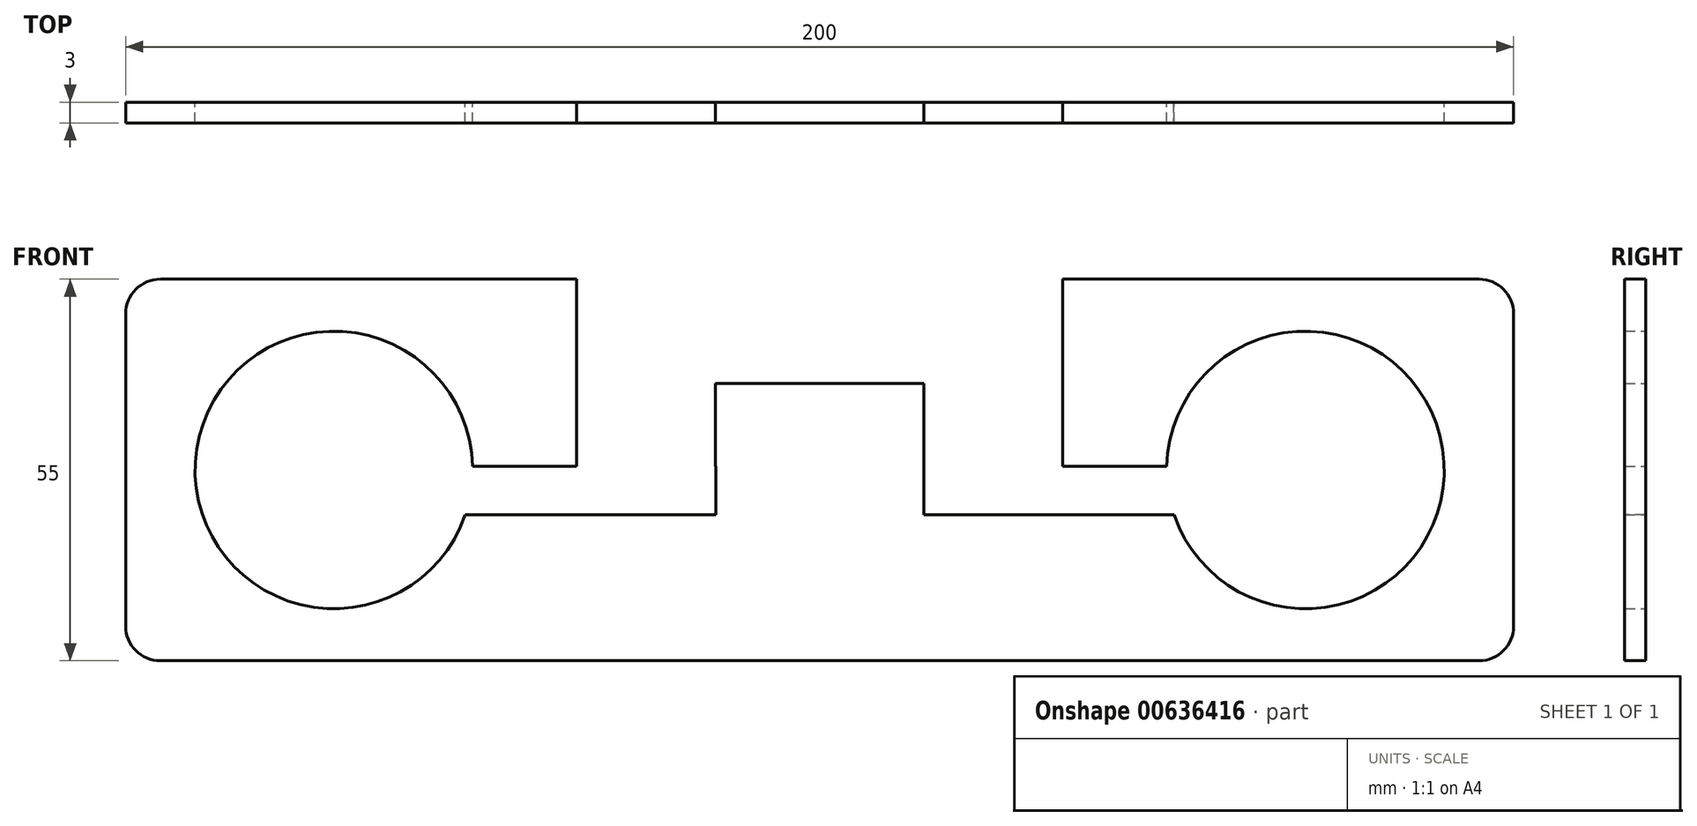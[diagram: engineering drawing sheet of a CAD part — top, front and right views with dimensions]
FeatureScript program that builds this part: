
annotation { "Feature Type Name" : "Feature", "Feature Type Description" : "" }
export const myFeature = defineFeature(function(context is Context, id is Id, definition is map)
    precondition{}
    {
        {
            var Q0;
            Q0=qCreatedBy(makeId("Front.planeOp"),FACE);
            var sketch = newSketch(context, id + "F0", { "sketchPlane" : qUnion([Q0])});
            skLineSegment(sketch, "E0.bottom", {"start": v(-79.88, 47.92) * mm, "end": v(110.12, 47.92) * mm});
            skLineSegment(sketch, "E0.top", {"start": v(-79.88, -7.08) * mm, "end": v(110.12, -7.08) * mm});
            skLineSegment(sketch, "E0.left", {"start": v(-84.88, 42.92) * mm, "end": v(-84.88, -2.08) * mm});
            skLineSegment(sketch, "E0.right", {"start": v(115.12, 42.92) * mm, "end": v(115.12, -2.08) * mm});
            skPoint(sketch, "E1.visualSharp", {"position": v(-84.88, 47.92) * mm});
            skArc(sketch, "E1.filletArc", {"start": v(-79.88, 47.92) * mm, "mid": v(-83.41, 46.45) * mm, "end": v(-84.88, 42.92) * mm});
            skPoint(sketch, "E2.visualSharp", {"position": v(115.12, 47.92) * mm});
            skArc(sketch, "E2.filletArc", {"start": v(115.12, 42.92) * mm, "mid": v(113.66, 46.45) * mm, "end": v(110.12, 47.92) * mm});
            skPoint(sketch, "E3.visualSharp", {"position": v(115.12, -7.08) * mm});
            skArc(sketch, "E3.filletArc", {"start": v(110.12, -7.08) * mm, "mid": v(113.66, -5.62) * mm, "end": v(115.12, -2.08) * mm});
            skPoint(sketch, "E4.visualSharp", {"position": v(-84.88, -7.08) * mm});
            skArc(sketch, "E4.filletArc", {"start": v(-84.88, -2.08) * mm, "mid": v(-83.41, -5.62) * mm, "end": v(-79.88, -7.08) * mm});
            skCircle(sketch, "E5", {"center": v(-54.88, 20.42) * mm, "radius": 20 * mm});
            skCircle(sketch, "E6", {"center": v(85.12, 20.42) * mm, "radius": 20 * mm});
            skSolve(sketch);
        }
        {
            var Q0;
            Q0=makeQuery(id+"F0.imprint","IMPRINT",FACE,{"disambiguationData":[TD([[makeQuery(id+"F0.imprint","IMPRINT",EDGE,{"derivedFrom":sQuery(id+"F0.wireOp",EDGE,"E0.bottom")}),-1.0]])]});
            extrude(context, id + "F1", {"entities" : qUnion([Q0]), "depth" : 3 * mm, "offsetDistance" : 25 * mm});
        }
        {
            var Q0;
            Q0=makeQuery(id+"F1.opExtrude","CAP_FACE",FACE,{"disambiguationData":[OSD([sQuery(id+"F0.wireOp",EDGE,"E0.bottom"),sQuery(id+"F0.wireOp",EDGE,"E0.top"),sQuery(id+"F0.wireOp",EDGE,"E0.left"),sQuery(id+"F0.wireOp",EDGE,"E0.right"),sQuery(id+"F0.wireOp",EDGE,"E1.filletArc"),sQuery(id+"F0.wireOp",EDGE,"E2.filletArc"),sQuery(id+"F0.wireOp",EDGE,"E3.filletArc"),sQuery(id+"F0.wireOp",EDGE,"E4.filletArc"),sQuery(id+"F0.wireOp",EDGE,"E5"),sQuery(id+"F0.wireOp",EDGE,"E6")])],"isStart":false});
            var sketch = newSketch(context, id + "F2", { "sketchPlane" : qUnion([Q0])});
            skLineSegment(sketch, "E7", {"start": v(-19.88, 47.92) * mm, "end": v(-19.88, 73.58) * mm});
            skLineSegment(sketch, "E8", {"start": v(50.12, 47.92) * mm, "end": v(50.12, 77.54) * mm});
            skSolve(sketch);
        }
        {
            var Q0;
            Q0=makeQuery(id+"F1.opExtrude","SWEPT_FACE",FACE,{"disambiguationData":[OSD([sQuery(id+"F0.wireOp",EDGE,"E0.bottom")])]});
            var sketch = newSketch(context, id + "F3", { "sketchPlane" : qUnion([Q0])});
            skLineSegment(sketch, "E9", {"start": v(-19.88, -3) * mm, "end": v(-19.88, 0) * mm});
            skLineSegment(sketch, "E10", {"start": v(50.12, -3) * mm, "end": v(50.12, 0) * mm});
            skSolve(sketch);
        }
        {
            var Q0;
            {var subQ0=sQuery(id+"F3.wireOp",EDGE,"E9");Q0=makeQuery(id+"F3.imprint","IMPRINT",FACE,{"disambiguationData":[TD([[makeQuery(id+"F3.imprint","IMPRINT",EDGE,{"derivedFrom":subQ0}),-1.0]])]});}
            extrude(context, id + "F4", {"entities" : qUnion([Q0]), "operationType" : NewBodyOperationType.REMOVE, "oppositeDirection" : true, "depth" : 15 * mm, "offsetDistance" : 25 * mm});
        }
        {
            var Q0;
            Q0=makeQuery(id+"F4.boolean.opBoolean","COPY",FACE,{"derivedFrom":makeQuery(id+"F4.opExtrude","CAP_FACE",FACE,{"disambiguationData":[OSD([sQuery(id+"F0.wireOp",EDGE,"E0.bottom"),sQuery(id+"F3.wireOp",EDGE,"E9"),sQuery(id+"F3.wireOp",EDGE,"E10")])],"isStart":false})});
            var sketch = newSketch(context, id + "F5", { "sketchPlane" : qUnion([Q0])});
            skLineSegment(sketch, "E11", {"start": v(0.12, -3) * mm, "end": v(0.12, 0) * mm});
            skLineSegment(sketch, "E12", {"start": v(30.12, 0) * mm, "end": v(30.12, -3) * mm});
            skSolve(sketch);
        }
        {
            var Q0;
            {var subQ0=sQuery(id+"F5.wireOp",EDGE,"E11");Q0=makeQuery(id+"F5.imprint","IMPRINT",FACE,{"disambiguationData":[TD([[makeQuery(id+"F5.imprint","IMPRINT",EDGE,{"derivedFrom":subQ0}),1.0]])]});}
            var Q1;
            {var subQ0=sQuery(id+"F5.wireOp",EDGE,"E12");Q1=makeQuery(id+"F5.imprint","IMPRINT",FACE,{"disambiguationData":[TD([[makeQuery(id+"F5.imprint","IMPRINT",EDGE,{"derivedFrom":subQ0}),1.0]])]});}
            extrude(context, id + "F6", {"entities" : qUnion([Q0, Q1]), "operationType" : NewBodyOperationType.REMOVE, "oppositeDirection" : true, "depth" : 12 * mm, "offsetDistance" : 25 * mm});
        }
        {
            var Q0;
            Q0=makeQuery(id+"F2.imprint","IMPRINT",FACE,{"disambiguationData":[TD([[makeQuery(id+"F2.imprint","IMPRINT",EDGE,{"derivedFrom":makeQuery(id+"F1.opExtrude","CAP_EDGE",EDGE,{"disambiguationData":[OSD([sQuery(id+"F0.wireOp",EDGE,"E0.top")])],"isStart":false})}),1.0]])]});
            var sketch = newSketch(context, id + "F7", { "sketchPlane" : qUnion([Q0])});
            skLineSegment(sketch, "E13", {"start": v(-19.86, 20.93) * mm, "end": v(-34.91, 20.93) * mm});
            skLineSegment(sketch, "E14", {"start": v(0.13, 20.94) * mm, "end": v(0.13, 13.94) * mm});
            skLineSegment(sketch, "E15", {"start": v(0.13, 13.94) * mm, "end": v(-36.02, 13.94) * mm});
            skLineSegment(sketch, "E16", {"start": v(50.12, 20.93) * mm, "end": v(65.14, 20.93) * mm});
            skLineSegment(sketch, "E17", {"start": v(30.12, 20.92) * mm, "end": v(30.12, 13.93) * mm});
            skLineSegment(sketch, "E18", {"start": v(30.12, 13.93) * mm, "end": v(66.08, 13.93) * mm});
            skLineSegment(sketch, "E19", {"start": v(-19.86, 20.93) * mm, "end": v(0.13, 20.94) * mm});
            skLineSegment(sketch, "E20", {"start": v(30.12, 20.92) * mm, "end": v(50.12, 20.93) * mm});
            skLineSegment(sketch, "E21", {"start": v(65.14, 20.93) * mm, "end": v(73.13, 16.83) * mm});
            skLineSegment(sketch, "E22", {"start": v(73.13, 16.83) * mm, "end": v(66.08, 13.93) * mm});
            skLineSegment(sketch, "E23", {"start": v(-34.91, 20.93) * mm, "end": v(-38.79, 20.93) * mm});
            skLineSegment(sketch, "E24", {"start": v(-38.79, 20.93) * mm, "end": v(-36.02, 13.94) * mm});
            skSolve(sketch);
        }
        {
            var Q0;
            Q0=qSketchRegion(id+"F7",true);
            extrude(context, id + "F8", {"entities" : qUnion([Q0]), "operationType" : NewBodyOperationType.REMOVE, "oppositeDirection" : true, "depth" : 25 * mm, "offsetDistance" : 25 * mm});
        }
    });
